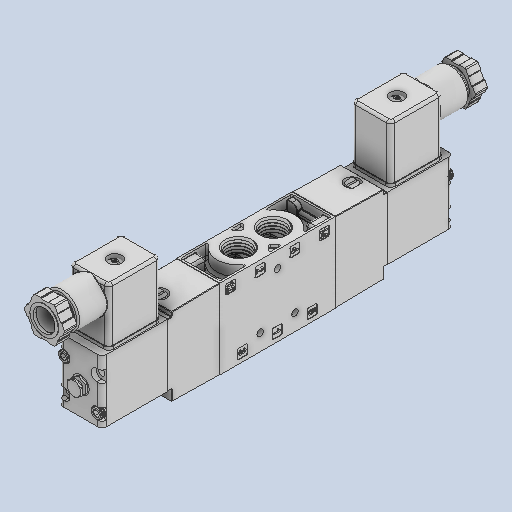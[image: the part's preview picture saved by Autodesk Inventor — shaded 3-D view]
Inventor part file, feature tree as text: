
AUTODESK INVENTOR PART (.ipt)
format: ipt  version: 2024.1 (Build 281209000, 209)  size: 4,756,480 bytes
history: native  units: in
note: dims shown in document units (in); Inventor stores cm internally (conversion verified against a paired STEP export)
features: other x23, fillet x2, mirror x2, pattern_circular x2, sketch x1
ambient origin geometry x8: Origin, YZ Plane, XZ Plane, XY Plane, X Axis, Y Axis, Z Axis, Center Point
bodies: Solid1 (feature_tree), Solid2 (feature_tree), Solid3 (feature_tree), Solid4 (feature_tree), Solid5 (feature_tree), Solid6 (feature_tree), Solid7 (feature_tree), Solid8 (feature_tree), Solid9 (feature_tree), Solid10 (feature_tree), Solid11 (feature_tree), Solid12 (feature_tree), Solid13 (feature_tree), Solid14 (feature_tree), Solid15 (feature_tree), Solid16 (feature_tree), Solid17 (feature_tree), Solid18 (feature_tree), Solid19 (feature_tree), Solid20 (feature_tree), Solid21 (feature_tree), Solid22 (feature_tree), Solid23 (feature_tree), Solid24 (feature_tree), Solid25 (feature_tree), Solid26 (feature_tree), Solid27 (feature_tree), Solid28 (feature_tree), Solid29 (feature_tree), Solid30 (feature_tree)
feature tree (30):
  other  "Boss-Extrude3"
  other  "Cut-Extrude6"
  other  "Cut-Extrude12"
  other  "CirPattern1[1]"
  other  "CirPattern1[2]"
  other  "CirPattern1[4]"
  other  "CirPattern1[5]"
  fillet  "Fillet13"  [1 undecoded]
  other  "Cut-Extrude30"
  other  "Boss-Extrude14"
  other  "Cut-Extrude32"
  other  "Cut-Extrude36"
  fillet  "Fillet14"  [1 undecoded]
  other  "CirPattern1[7]"
  other  "CirPattern1[8]"
  other  "CirPattern1[9]"
  other  "CirPattern1[11]"
  other  "CirPattern1[12]"
  other  "Cut-Extrude44"
  other  "Cut-Extrude47[1]"
  other  "Cut-Extrude47[2]"
  mirror  "Mirror2[1]"
  mirror  "Mirror2[2]"
  other  "Boss-Extrude19"
  pattern_circular  "CirPattern4"
  other  "Boss-Extrude21"
  pattern_circular  "CirPattern5"
  sketch  "Sketch-Pattern2"
  other  "CirPattern6[1]"
  other  "CirPattern6[2]"
note: 2 required parameter values undecoded (feature->parameter linkage not recoverable at this tier; creation-order binding heuristic only, values carry confidence <= 0.55)
